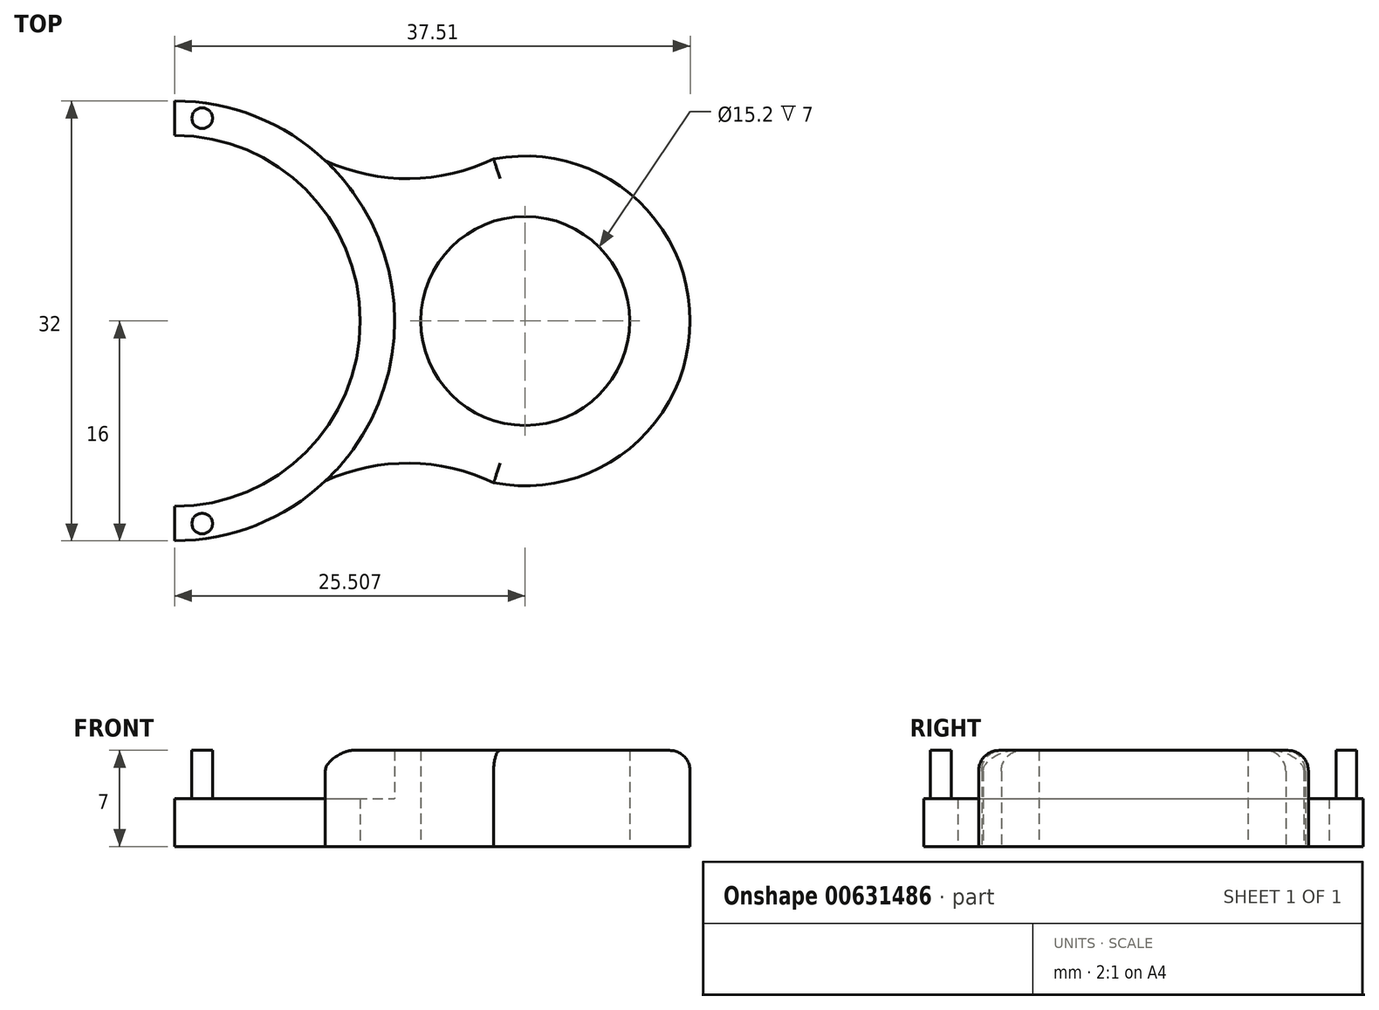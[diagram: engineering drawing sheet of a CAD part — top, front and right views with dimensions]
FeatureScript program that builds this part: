
annotation { "Feature Type Name" : "Feature", "Feature Type Description" : "" }
export const myFeature = defineFeature(function(context is Context, id is Id, definition is map)
    precondition{}
    {
        {
            var Q0;
            Q0=qCreatedBy(makeId("Top.planeOp"),FACE);
            var sketch = newSketch(context, id + "F0", { "sketchPlane" : qUnion([Q0])});
            skCircle(sketch, "E0", {"center": v(0, 0) * mm, "radius": 11.12 * mm});
            skCircle(sketch, "E1", {"center": v(0, 0) * mm, "radius": 16 * mm});
            skLineSegment(sketch, "E2", {"start": v(0, 0) * mm, "end": v(34.83, 0) * mm, "construction": true});
            skCircle(sketch, "E3", {"center": v(25.5, 0) * mm, "radius": 7.6 * mm});
            skArc(sketch, "E4", {"start": v(20.04, -10.68) * mm, "mid": v(37.5, 0) * mm, "end": v(20.04, 10.68) * mm});
            skArc(sketch, "E5", {"start": v(23.21, -11.78) * mm, "mid": v(17.1, -10.35) * mm, "end": v(10.96, -11.66) * mm});
            skArc(sketch, "E6.MirrorCS", {"start": v(23.21, 11.78) * mm, "mid": v(17.1, 10.35) * mm, "end": v(10.96, 11.66) * mm});
            skLineSegment(sketch, "E7.MirrorCS", {"start": v(0, 0) * mm, "end": v(-34.83, 0) * mm, "construction": true});
            skCircle(sketch, "E8.MirrorC", {"center": v(-25.5, 0) * mm, "radius": 7.6 * mm});
            skArc(sketch, "E9.MirrorC", {"start": v(-20.04, -10.68) * mm, "mid": v(-37.5, 0) * mm, "end": v(-20.04, 10.68) * mm});
            skArc(sketch, "E10.MirrorCS", {"start": v(-23.21, -11.78) * mm, "mid": v(-17.1, -10.35) * mm, "end": v(-10.96, -11.66) * mm});
            skArc(sketch, "E11.MirrorCS", {"start": v(-23.21, 11.78) * mm, "mid": v(-17.1, 10.35) * mm, "end": v(-10.96, 11.66) * mm});
            skLineSegment(sketch, "E12", {"start": v(0, -16) * mm, "end": v(0, -13.5) * mm});
            skLineSegment(sketch, "E13", {"start": v(0, 16) * mm, "end": v(0, 13.5) * mm});
            skArc(sketch, "E14", {"start": v(0, -13.5) * mm, "mid": v(13.5, 0) * mm, "end": v(0, 13.5) * mm});
            skCircle(sketch, "E15", {"center": v(2, 14.75) * mm, "radius": 0.75 * mm});
            skPoint(sketch, "E16.endSnap0", {"position": v(0, -14.75) * mm});
            skCircle(sketch, "E17", {"center": v(2, -14.75) * mm, "radius": 0.75 * mm});
            skSolve(sketch);
        }
        {
            var Q0;
            Q0=makeQuery(id+"F0.imprint","IMPRINT",FACE,{"disambiguationData":[TD([[makeQuery(id+"F0.imprint","IMPRINT",EDGE,{"derivedFrom":sQuery(id+"F0.wireOp",EDGE,"E3")}),-1.0]])]});
            extrude(context, id + "F1", {"entities" : qUnion([Q0]), "depth" : 7 * mm, "offsetDistance" : 25 * mm});
        }
        {
            var Q0;
            {var subQ0=sQuery(id+"F0.wireOp",EDGE,"E12");Q0=makeQuery(id+"F0.imprint","IMPRINT",FACE,{"disambiguationData":[TD([[makeQuery(id+"F0.imprint","IMPRINT",EDGE,{"derivedFrom":subQ0}),-1.0]])]});}
            extrude(context, id + "F2", {"entities" : qUnion([Q0]), "operationType" : NewBodyOperationType.ADD, "depth" : 3.5 * mm, "offsetDistance" : 25 * mm});
        }
        {
            var Q0;
            Q0=makeQuery(id+"F0.imprint","IMPRINT",FACE,{"disambiguationData":[TD([[makeQuery(id+"F0.imprint","IMPRINT",EDGE,{"derivedFrom":sQuery(id+"F0.wireOp",EDGE,"E17")}),1.0]])]});
            var Q1;
            Q1=makeQuery(id+"F0.imprint","IMPRINT",FACE,{"disambiguationData":[TD([[makeQuery(id+"F0.imprint","IMPRINT",EDGE,{"derivedFrom":sQuery(id+"F0.wireOp",EDGE,"E15")}),1.0]])]});
            extrude(context, id + "F3", {"entities" : qUnion([Q0, Q1]), "operationType" : NewBodyOperationType.ADD, "depth" : 7 * mm, "offsetDistance" : 25 * mm});
        }
        {
            var Q0;
            Q0=makeQuery(id+"F1.opExtrude","CAP_EDGE",EDGE,{"disambiguationData":[OSD([sQuery(id+"F0.wireOp",EDGE,"E4")])],"isStart":false});
            var Q1;
            Q1=makeQuery(id+"F1.opExtrude","CAP_EDGE",EDGE,{"disambiguationData":[OSD([sQuery(id+"F0.wireOp",EDGE,"E6.MirrorCS")])],"isStart":false});
            var Q2;
            Q2=makeQuery(id+"F1.opExtrude","CAP_EDGE",EDGE,{"disambiguationData":[OSD([sQuery(id+"F0.wireOp",EDGE,"E5")])],"isStart":false});
            fillet(context, id + "F4", {"entities" : qUnion([Q0, Q1, Q2]), "radius" : 1.5 * mm, "tangentPropagation" : true, "allowEdgeOverflow" : false});
        }
    });
